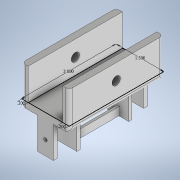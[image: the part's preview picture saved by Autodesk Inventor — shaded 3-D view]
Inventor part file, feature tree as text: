
AUTODESK INVENTOR PART (.ipt)
format: ipt  version: 2020 (Build 240168000, 168)  size: 641,536 bytes
history: native  units: in
note: dims shown in document units (in); Inventor stores cm internally (conversion verified against a paired STEP export)
features: sketch x5, extrude x5, hole x2, fillet x1
ambient origin geometry x8: Origin, YZ Plane, XZ Plane, XY Plane, X Axis, Y Axis, Z Axis, Center Point
bodies: Solid1 (feature_tree)
feature tree (13):
  sketch  "Sketch1"  dims[d0=1.5in d1=3.0in]
  extrude  "Extrusion1"  Depth=3.0in
  extrude  "Extrusion2"  Depth=0.2in
  hole  "Hole1"  [1 undecoded]
  extrude  "Extrusion3"  Depth=0.5in
  hole  "Hole2"  [1 undecoded]
  fillet  "Fillet1"  Radius=0.75in
  extrude  "Extrusion4"  Depth=0.125in
  extrude  "Extrusion5"  Depth=0.125in
  sketch  "Sketch2"  dims[d2=0.2in d3=0.2in]
  sketch  "Sketch3"  dims[d4=1.0in d5=0.0in d6=0.2in d7=0.0in]
  sketch  "Sketch5"  dims[d8=0.5in]
  sketch  "Sketch6"  dims[d9=0.266in d10=0.75in d11=0.438in d12=0.25in d13=0.5635in d14=1.0in d15=0.8108in d16=0.5in d17=1.0in d18=0.75in d19=0.125in d20=0.125in d21=1.0in d22=0.0in d23=0.45in d24=0.1125in d25=0.75in d26=0.438in d27=0.25in d28=0.5635in d29=1.0in d30=0.8108in d31=0.125in d32=0.125in d33=0.125in d34=0.5in d35=0.5in d36=90.0deg d37=0.1in d38=0.1in d39=0.125in d40=0.075in d41=0.25in d42=1.6in d43=0.0in d44=0.05in d45=0.0in d46=0.5in d47=0.5in d48=0.5in d49=0.375in]
note: 2 required parameter values undecoded (feature->parameter linkage not recoverable at this tier; creation-order binding heuristic only, values carry confidence <= 0.55)
